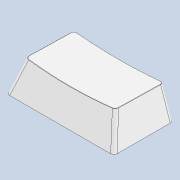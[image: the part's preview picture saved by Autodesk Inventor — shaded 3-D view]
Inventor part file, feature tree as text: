
AUTODESK INVENTOR PART (.ipt)
format: ipt  version: 2021 (Build 250183000, 183)  size: 224,256 bytes
history: native  units: in
note: dims shown in document units (in); Inventor stores cm internally (conversion verified against a paired STEP export)
features: chamfer x1
ambient origin geometry x8: Origin, YZ Plane, XZ Plane, XY Plane, X Axis, Y Axis, Z Axis, Center Point
bodies: Solid1 (feature_tree)
feature tree (1):
  chamfer  "Chamfer1"  [1 undecoded]
note: 1 required parameter value undecoded (feature->parameter linkage not recoverable at this tier; creation-order binding heuristic only, values carry confidence <= 0.55)
